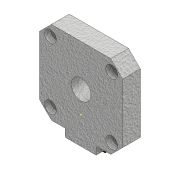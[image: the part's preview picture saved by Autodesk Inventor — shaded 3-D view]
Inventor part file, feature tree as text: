
AUTODESK INVENTOR PART (.ipt)
format: ipt  version: 2018 (Build 220112000, 112)  size: 224,256 bytes
history: native  units: mm
features: sketch x9, extrude x7, mirror x4, projected_geometry x3, chamfer x1, fillet x1
ambient origin geometry x8: Origin, YZ Plane, XZ Plane, XY Plane, X Axis, Y Axis, Z Axis, Center Point
bodies: Solid1 (feature_tree)
feature tree (25):
  extrude  "Extrusion1"  Depth=42.0mm
  chamfer  "Chamfer1"  Distance=9.0mm
  sketch  "Sketch2"  dims[d4=6.0mm d5=2.0mm d6=45.0deg d7=10.0mm]
  extrude  "Extrusion2"  Depth=10.0mm
  extrude  "Extrusion3"  Depth=3.0mm
  mirror  "Mirror1"
  mirror  "Mirror2"
  extrude  "Extrusion5"  Depth=5.5mm
  fillet  "Fillet1"  Radius=22.0mm
  extrude  "Extrusion6"  Depth=16.0mm
  extrude  "Extrusion7"  Depth=4.0mm
  sketch  "Sketch9"  dims[d28=0.5mm]
  extrude  "Extrusion8"  Depth=10.0mm TaperAngle=0.0deg
  mirror  "Mirror3"
  mirror  "Mirror4"
  sketch  "Sketch1"  dims[d0=42.0mm d1=42.0mm d2=9.0mm d3=0.0mm]
  sketch  "Sketch3"  dims[d8=22.0mm d9=0.0mm d10=3.0mm]
  sketch  "Sketch4"  dims[d11=5.5mm d12=5.5mm d13=22.0mm d14=0.0mm]
  sketch  "Sketch6"  dims[d20=16.0mm d21=8.0mm]
  projected_geometry  "Projected Loop1"
  sketch  "Sketch7"  dims[d22=4.0mm d23=0.0mm d24=4.0mm]
  projected_geometry  "Projected Loop2"
  sketch  "Sketch8"  dims[d25=0.5mm d26=10.0mm d27=0.0mm]
  projected_geometry  "Projected Loop3"
  sketch  "Sketch10"  dims[d29=0.2mm d30=15.0mm d31=0.0mm d32=6.0mm d33=3.0mm d34=0.0mm]
